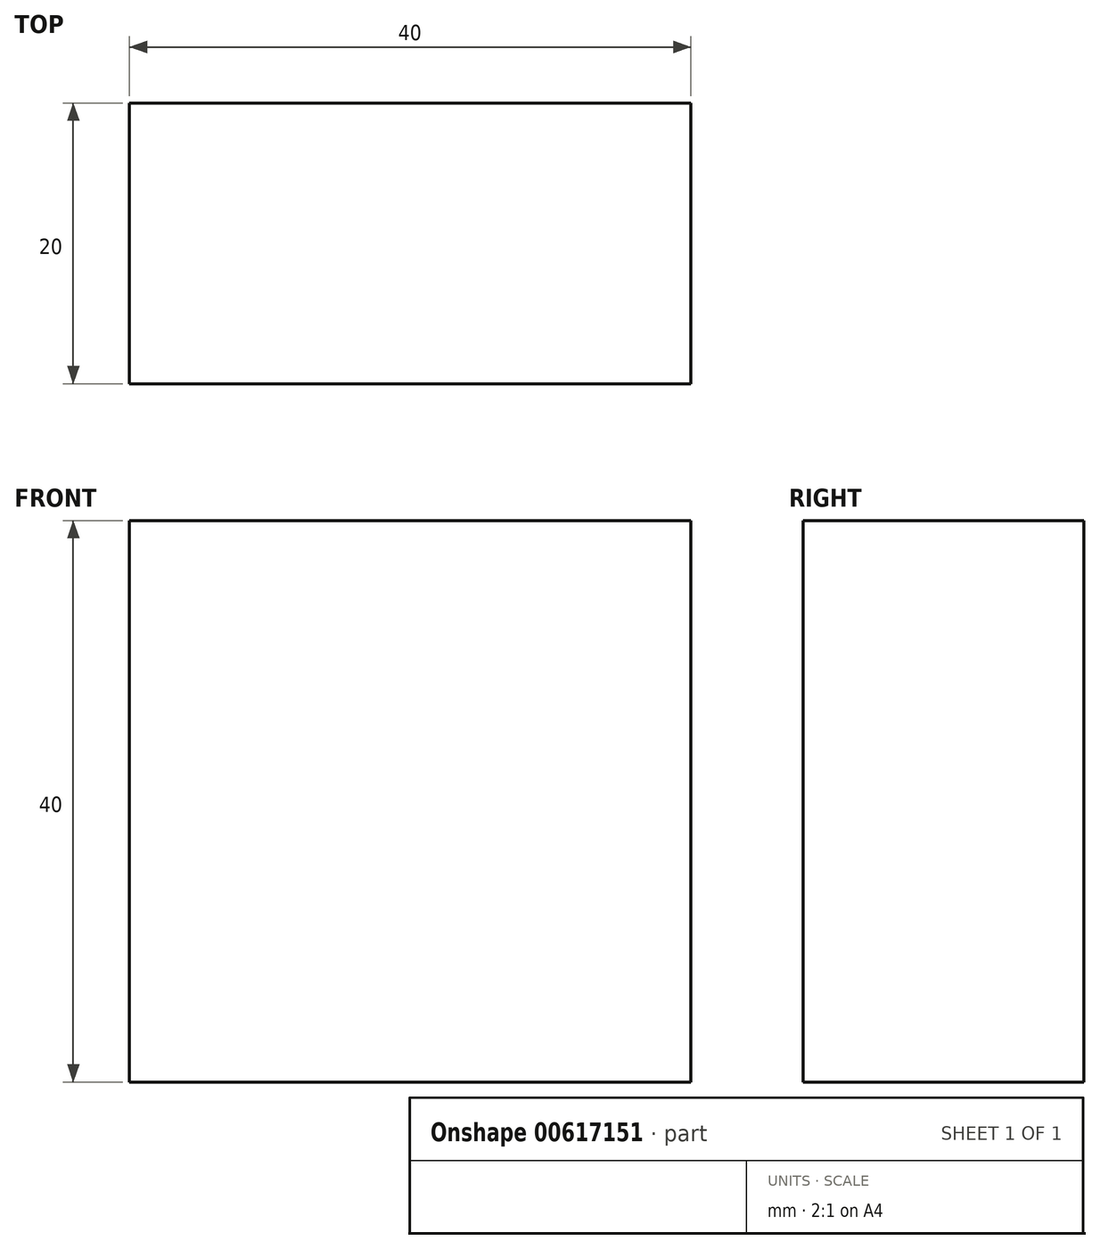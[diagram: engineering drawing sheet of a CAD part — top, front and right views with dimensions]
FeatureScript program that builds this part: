
annotation { "Feature Type Name" : "Feature", "Feature Type Description" : "" }
export const myFeature = defineFeature(function(context is Context, id is Id, definition is map)
    precondition{}
    {
        {
            var Q0;
            Q0=qCreatedBy(makeId("Front.planeOp"),FACE);
            var sketch = newSketch(context, id + "F0", { "sketchPlane" : qUnion([Q0])});
            skLineSegment(sketch, "E0", {"start": v(-41.45, 26.06) * mm, "end": v(-1.45, 26.06) * mm});
            skLineSegment(sketch, "E1", {"start": v(-1.45, 26.06) * mm, "end": v(-1.45, -13.94) * mm});
            skLineSegment(sketch, "E2", {"start": v(-1.45, -13.94) * mm, "end": v(-41.45, -13.94) * mm});
            skLineSegment(sketch, "E3", {"start": v(-41.45, 26.06) * mm, "end": v(-41.45, -13.94) * mm});
            skSolve(sketch);
        }
        {
            var Q0;
            Q0 = qSketchRegion(id + "F0", true);
            extrude(context, id + "F1", {"entities" : qUnion([Q0]), "depth" : 20 * mm, "offsetDistance" : 25 * mm});
        }
    });
